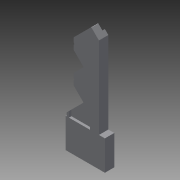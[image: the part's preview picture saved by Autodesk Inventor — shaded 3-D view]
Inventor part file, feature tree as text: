
AUTODESK INVENTOR PART (.ipt)
format: ipt  version: 2013 (Build 170138000, 138)  size: 174,592 bytes
history: native  units: mm
features: extrude x4, sketch x4, other x2, fillet x1
ambient origin geometry x8: Origin, YZ Plane, XZ Plane, XY Plane, X Axis, Y Axis, Z Axis, Center Point
feature tree (11):
  other  "ソリッド1"
  extrude  "押し出し1"  Depth=8.9mm
  extrude  "押し出し3"  Depth=24.0mm
  extrude  "押し出し4"  Depth=4.45mm
  extrude  "押し出し5"  Depth=12.0mm
  fillet  "フィレット1"  Radius=1.9mm
  sketch  "スケッチ1"
  sketch  "スケッチ2"
  sketch  "スケッチ3"
  sketch  "スケッチ4"
  other  "断面エッジを投影1"
